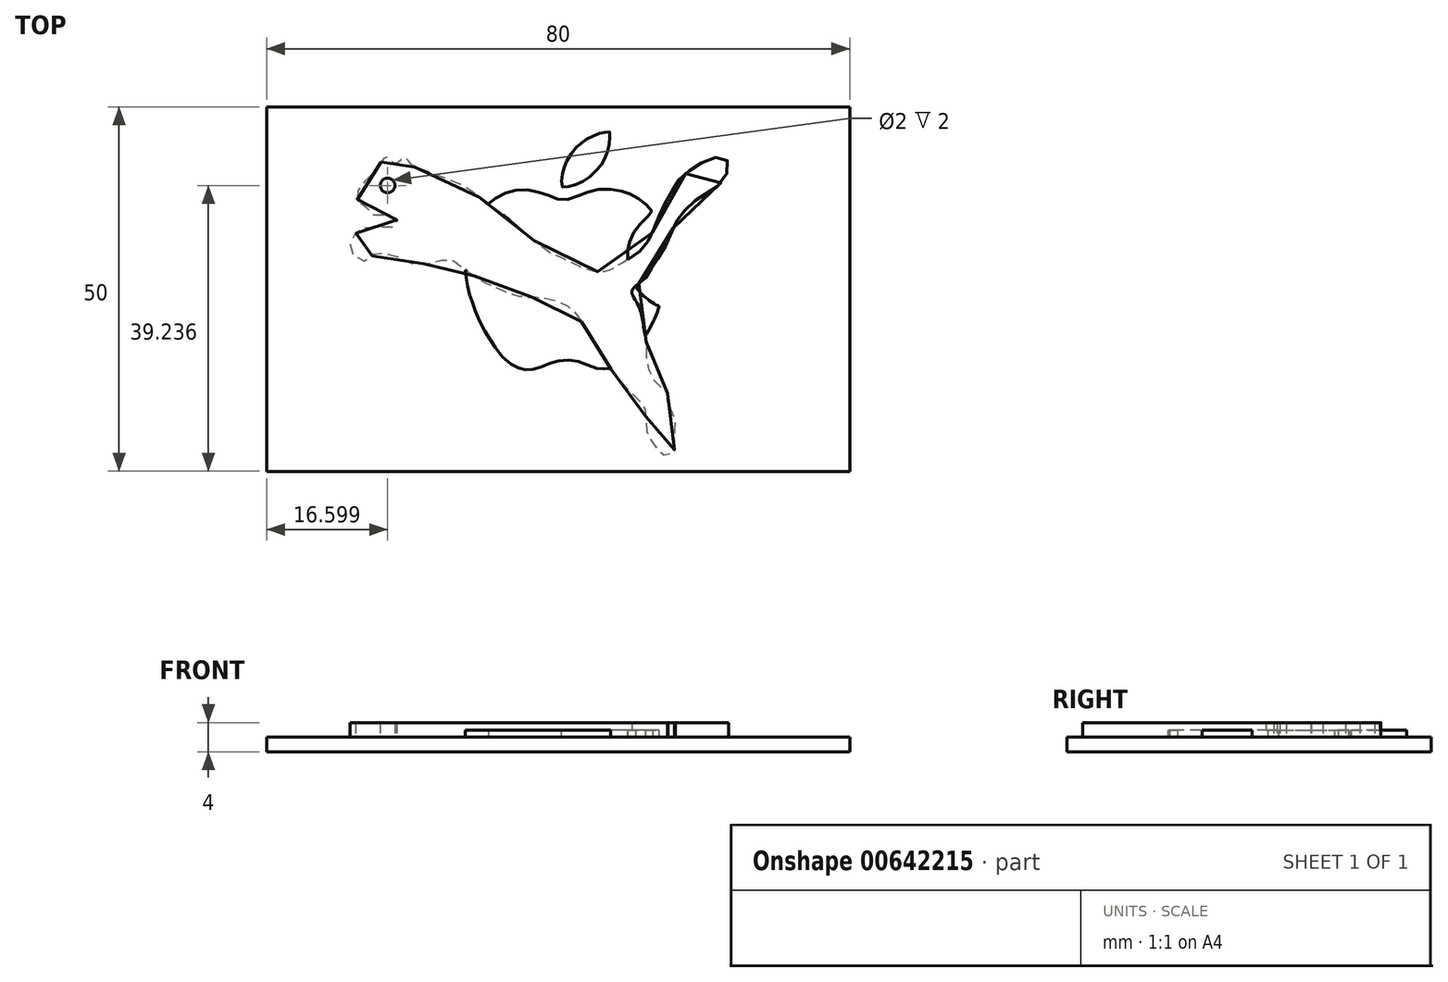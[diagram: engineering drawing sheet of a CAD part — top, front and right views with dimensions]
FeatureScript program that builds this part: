
annotation { "Feature Type Name" : "Feature", "Feature Type Description" : "" }
export const myFeature = defineFeature(function(context is Context, id is Id, definition is map)
    precondition{}
    {
        {
            var Q0;
            Q0=qCreatedBy(makeId("Top.planeOp"),FACE);
            var sketch = newSketch(context, id + "F0", { "sketchPlane" : qUnion([Q0])});
            skFitSpline(sketch, "E0", {"points": [v(-22.96, 25.7) * mm, v(-24.03, 24.14) * mm, v(-25, 23.44) * mm, v(-25.24, 22.78) * mm, v(-25.97, 21.9) * mm, v(-26.4, 21.24) * mm, v(-26.11, 20.44) * mm, v(-25.38, 19.78) * mm, v(-24.65, 19.13) * mm, v(-24.01, 18.5) * mm, v(-22.1, 18.4) * mm, v(-20.93, 18.18) * mm, v(-20.78, 17.23) * mm, v(-21, 16.79) * mm, v(-22.17, 16.79) * mm, v(-24, 16.72) * mm, v(-25.09, 16.64) * mm, v(-26.11, 16.06) * mm, v(-26.84, 15.55) * mm, v(-27.2, 14.38) * mm, v(-26.99, 13.14) * mm, v(-26.11, 12.48) * mm, v(-24.94, 12.12) * mm, v(-24.07, 12.92) * mm, v(-23.63, 13.36) * mm, v(-21.84, 13.01) * mm, v(-20.44, 12.57) * mm, v(-18.88, 11.82) * mm, v(-16.72, 11.72) * mm, v(-15.1, 12.05) * mm, v(-13.48, 12.48) * mm, v(-12.31, 11.53) * mm, v(-10.93, 10.58) * mm, v(-9.68, 9.7) * mm, v(-8.22, 8.9) * mm, v(-6.18, 8.03) * mm, v(-4.14, 7.3) * mm, v(-1.87, 7.15) * mm, v(0, 6.93) * mm, v(1.7, 6.42) * mm, v(3.16, 5.55) * mm, v(4.19, 4.3) * mm, v(5.06, 3) * mm, v(6.01, 1.31) * mm, v(6.82, 0) * mm, v(7.7, -1.39) * mm, v(8.5, -2.56) * mm, v(9.55, -3.97) * mm, v(10.78, -5.38) * mm, v(12.45, -7.06) * mm, v(13.25, -8.11) * mm, v(13.42, -10.14) * mm, v(13.69, -11.81) * mm, v(14.66, -13.22) * mm, v(15.63, -14.46) * mm, v(17.12, -14.2) * mm, v(17.3, -12.43) * mm, v(17.48, -10.5) * mm, v(17.12, -8.82) * mm, v(16.42, -7.59) * mm, v(16.33, -5.91) * mm, v(15.45, -5.2) * mm, v(14.4, -4.15) * mm, v(13.6, -1.86) * mm, v(13.51, 0) * mm, v(13.25, 2.1) * mm, v(12.9, 4.22) * mm, v(12.28, 6.16) * mm, v(11.49, 8) * mm, v(13.06, 9.5) * mm, v(14.01, 10.81) * mm, v(14.82, 12.13) * mm, v(16.36, 14.66) * mm, v(17.3, 17.03) * mm, v(18.38, 18.6) * mm, v(20.24, 20.48) * mm, v(21.9, 21.47) * mm, v(24.13, 23.39) * mm, v(24.63, 25.82) * mm, v(22.75, 26.26) * mm, v(20.08, 24.99) * mm, v(18.17, 23.5) * mm, v(16.9, 21.58) * mm, v(15.61, 19.24) * mm, v(14.76, 17.22) * mm, v(13.7, 14.77) * mm, v(12.1, 13.07) * mm, v(9.55, 11.47) * mm, v(7.5, 10.6) * mm, v(4.01, 11.47) * mm, v(1.35, 12.75) * mm, v(0, 13.39) * mm, v(-1.73, 14.77) * mm, v(-3.14, 15.83) * mm, v(-5.35, 17.75) * mm, v(-7.37, 19.35) * mm, v(-9.66, 21.04) * mm, v(-11.63, 22.43) * mm, v(-13.97, 23.39) * mm, v(-16.74, 24.45) * mm, v(-18.87, 25.41) * mm, v(-19.61, 26.26) * mm, v(-20.46, 25.73) * mm, v(-21.12, 25.53) * mm, v(-21.8, 26) * mm, v(-22.25, 26.34) * mm, v(-22.96, 25.7) * mm]});
            skCircle(sketch, "E1", {"center": v(-22.04, 22.48) * mm, "radius": 0.08 * mm});
            skSolve(sketch);
        }
        {
            var Q0;
            Q0 = qSketchRegion(id + "F0", true);
            extrude(context, id + "F1", {"entities" : qUnion([Q0]), "depth" : 4 * mm, "offsetDistance" : 25 * mm});
        }
        {
            var Q0;
            Q0=sQuery(id+"F0.wireOp",VERTEX,"E1.center");
            var Q1;
            Q1=makeQuery(id+"F1.opExtrude","SWEPT_BODY",BODY,{"disambiguationData":[OSD([sQuery(id+"F0.wireOp",EDGE,"E0"),sQuery(id+"F0.wireOp",EDGE,"b66a4d29-bf38-48c4-a418-0a1d268e2e5a.sketch_text.stroke-0"),sQuery(id+"F0.wireOp",EDGE,"b66a4d29-bf38-48c4-a418-0a1d268e2e5a.sketch_text.stroke-1"),sQuery(id+"F0.wireOp",EDGE,"b66a4d29-bf38-48c4-a418-0a1d268e2e5a.sketch_text.stroke-2"),sQuery(id+"F0.wireOp",EDGE,"b66a4d29-bf38-48c4-a418-0a1d268e2e5a.sketch_text.stroke-3"),sQuery(id+"F0.wireOp",EDGE,"b66a4d29-bf38-48c4-a418-0a1d268e2e5a.sketch_text.stroke-4"),sQuery(id+"F0.wireOp",EDGE,"b66a4d29-bf38-48c4-a418-0a1d268e2e5a.sketch_text.stroke-5"),sQuery(id+"F0.wireOp",EDGE,"b66a4d29-bf38-48c4-a418-0a1d268e2e5a.sketch_text.stroke-6"),sQuery(id+"F0.wireOp",EDGE,"b66a4d29-bf38-48c4-a418-0a1d268e2e5a.sketch_text.stroke-7"),sQuery(id+"F0.wireOp",EDGE,"b66a4d29-bf38-48c4-a418-0a1d268e2e5a.sketch_text.stroke-8"),sQuery(id+"F0.wireOp",EDGE,"b66a4d29-bf38-48c4-a418-0a1d268e2e5a.sketch_text.stroke-9"),sQuery(id+"F0.wireOp",EDGE,"b66a4d29-bf38-48c4-a418-0a1d268e2e5a.sketch_text.stroke-10"),sQuery(id+"F0.wireOp",EDGE,"b66a4d29-bf38-48c4-a418-0a1d268e2e5a.sketch_text.stroke-11"),sQuery(id+"F0.wireOp",EDGE,"b66a4d29-bf38-48c4-a418-0a1d268e2e5a.sketch_text.stroke-12"),sQuery(id+"F0.wireOp",EDGE,"b66a4d29-bf38-48c4-a418-0a1d268e2e5a.sketch_text.stroke-13"),sQuery(id+"F0.wireOp",EDGE,"b66a4d29-bf38-48c4-a418-0a1d268e2e5a.sketch_text.stroke-14"),sQuery(id+"F0.wireOp",EDGE,"b66a4d29-bf38-48c4-a418-0a1d268e2e5a.sketch_text.stroke-15"),sQuery(id+"F0.wireOp",EDGE,"b66a4d29-bf38-48c4-a418-0a1d268e2e5a.sketch_text.stroke-23"),sQuery(id+"F0.wireOp",EDGE,"b66a4d29-bf38-48c4-a418-0a1d268e2e5a.sketch_text.stroke-24"),sQuery(id+"F0.wireOp",EDGE,"b66a4d29-bf38-48c4-a418-0a1d268e2e5a.sketch_text.stroke-25"),sQuery(id+"F0.wireOp",EDGE,"b66a4d29-bf38-48c4-a418-0a1d268e2e5a.sketch_text.stroke-26"),sQuery(id+"F0.wireOp",EDGE,"b66a4d29-bf38-48c4-a418-0a1d268e2e5a.sketch_text.stroke-27"),sQuery(id+"F0.wireOp",EDGE,"b66a4d29-bf38-48c4-a418-0a1d268e2e5a.sketch_text.stroke-28"),sQuery(id+"F0.wireOp",EDGE,"b66a4d29-bf38-48c4-a418-0a1d268e2e5a.sketch_text.stroke-29"),sQuery(id+"F0.wireOp",EDGE,"b66a4d29-bf38-48c4-a418-0a1d268e2e5a.sketch_text.stroke-30"),sQuery(id+"F0.wireOp",EDGE,"b66a4d29-bf38-48c4-a418-0a1d268e2e5a.sketch_text.stroke-31"),sQuery(id+"F0.wireOp",EDGE,"b66a4d29-bf38-48c4-a418-0a1d268e2e5a.sketch_text.stroke-32"),sQuery(id+"F0.wireOp",EDGE,"b66a4d29-bf38-48c4-a418-0a1d268e2e5a.sketch_text.stroke-33"),sQuery(id+"F0.wireOp",EDGE,"b66a4d29-bf38-48c4-a418-0a1d268e2e5a.sketch_text.stroke-34"),sQuery(id+"F0.wireOp",EDGE,"b66a4d29-bf38-48c4-a418-0a1d268e2e5a.sketch_text.stroke-35"),sQuery(id+"F0.wireOp",EDGE,"b66a4d29-bf38-48c4-a418-0a1d268e2e5a.sketch_text.stroke-36"),sQuery(id+"F0.wireOp",EDGE,"b66a4d29-bf38-48c4-a418-0a1d268e2e5a.sketch_text.stroke-37"),sQuery(id+"F0.wireOp",EDGE,"b66a4d29-bf38-48c4-a418-0a1d268e2e5a.sketch_text.stroke-38"),sQuery(id+"F0.wireOp",EDGE,"b66a4d29-bf38-48c4-a418-0a1d268e2e5a.sketch_text.stroke-39"),sQuery(id+"F0.wireOp",EDGE,"b66a4d29-bf38-48c4-a418-0a1d268e2e5a.sketch_text.stroke-40"),sQuery(id+"F0.wireOp",EDGE,"b66a4d29-bf38-48c4-a418-0a1d268e2e5a.sketch_text.stroke-41"),sQuery(id+"F0.wireOp",EDGE,"b66a4d29-bf38-48c4-a418-0a1d268e2e5a.sketch_text.stroke-42"),sQuery(id+"F0.wireOp",EDGE,"b66a4d29-bf38-48c4-a418-0a1d268e2e5a.sketch_text.stroke-43"),sQuery(id+"F0.wireOp",EDGE,"b66a4d29-bf38-48c4-a418-0a1d268e2e5a.sketch_text.stroke-44"),sQuery(id+"F0.wireOp",EDGE,"b66a4d29-bf38-48c4-a418-0a1d268e2e5a.sketch_text.stroke-45"),sQuery(id+"F0.wireOp",EDGE,"b66a4d29-bf38-48c4-a418-0a1d268e2e5a.sketch_text.stroke-46"),sQuery(id+"F0.wireOp",EDGE,"b66a4d29-bf38-48c4-a418-0a1d268e2e5a.sketch_text.stroke-47"),sQuery(id+"F0.wireOp",EDGE,"b66a4d29-bf38-48c4-a418-0a1d268e2e5a.sketch_text.stroke-48"),sQuery(id+"F0.wireOp",EDGE,"b66a4d29-bf38-48c4-a418-0a1d268e2e5a.sketch_text.stroke-49"),sQuery(id+"F0.wireOp",EDGE,"b66a4d29-bf38-48c4-a418-0a1d268e2e5a.sketch_text.stroke-50"),sQuery(id+"F0.wireOp",EDGE,"b66a4d29-bf38-48c4-a418-0a1d268e2e5a.sketch_text.stroke-51"),sQuery(id+"F0.wireOp",EDGE,"b66a4d29-bf38-48c4-a418-0a1d268e2e5a.sketch_text.stroke-52"),sQuery(id+"F0.wireOp",EDGE,"b66a4d29-bf38-48c4-a418-0a1d268e2e5a.sketch_text.stroke-53"),sQuery(id+"F0.wireOp",EDGE,"b66a4d29-bf38-48c4-a418-0a1d268e2e5a.sketch_text.stroke-54"),sQuery(id+"F0.wireOp",EDGE,"b66a4d29-bf38-48c4-a418-0a1d268e2e5a.sketch_text.stroke-55"),sQuery(id+"F0.wireOp",EDGE,"b66a4d29-bf38-48c4-a418-0a1d268e2e5a.sketch_text.stroke-56"),sQuery(id+"F0.wireOp",EDGE,"b66a4d29-bf38-48c4-a418-0a1d268e2e5a.sketch_text.stroke-57"),sQuery(id+"F0.wireOp",EDGE,"b66a4d29-bf38-48c4-a418-0a1d268e2e5a.sketch_text.stroke-58"),sQuery(id+"F0.wireOp",EDGE,"b66a4d29-bf38-48c4-a418-0a1d268e2e5a.sketch_text.stroke-59"),sQuery(id+"F0.wireOp",EDGE,"b66a4d29-bf38-48c4-a418-0a1d268e2e5a.sketch_text.stroke-60"),sQuery(id+"F0.wireOp",EDGE,"b66a4d29-bf38-48c4-a418-0a1d268e2e5a.sketch_text.stroke-61"),sQuery(id+"F0.wireOp",EDGE,"b66a4d29-bf38-48c4-a418-0a1d268e2e5a.sketch_text.stroke-62"),sQuery(id+"F0.wireOp",EDGE,"b66a4d29-bf38-48c4-a418-0a1d268e2e5a.sketch_text.stroke-63"),sQuery(id+"F0.wireOp",EDGE,"b66a4d29-bf38-48c4-a418-0a1d268e2e5a.sketch_text.stroke-64"),sQuery(id+"F0.wireOp",EDGE,"b66a4d29-bf38-48c4-a418-0a1d268e2e5a.sketch_text.stroke-65"),sQuery(id+"F0.wireOp",EDGE,"b66a4d29-bf38-48c4-a418-0a1d268e2e5a.sketch_text.stroke-66"),sQuery(id+"F0.wireOp",EDGE,"b66a4d29-bf38-48c4-a418-0a1d268e2e5a.sketch_text.stroke-67"),sQuery(id+"F0.wireOp",EDGE,"b66a4d29-bf38-48c4-a418-0a1d268e2e5a.sketch_text.stroke-68"),sQuery(id+"F0.wireOp",EDGE,"b66a4d29-bf38-48c4-a418-0a1d268e2e5a.sketch_text.stroke-69"),sQuery(id+"F0.wireOp",EDGE,"b66a4d29-bf38-48c4-a418-0a1d268e2e5a.sketch_text.stroke-70"),sQuery(id+"F0.wireOp",EDGE,"b66a4d29-bf38-48c4-a418-0a1d268e2e5a.sketch_text.stroke-71"),sQuery(id+"F0.wireOp",EDGE,"b66a4d29-bf38-48c4-a418-0a1d268e2e5a.sketch_text.stroke-72"),sQuery(id+"F0.wireOp",EDGE,"b66a4d29-bf38-48c4-a418-0a1d268e2e5a.sketch_text.stroke-73"),sQuery(id+"F0.wireOp",EDGE,"b66a4d29-bf38-48c4-a418-0a1d268e2e5a.sketch_text.stroke-74"),sQuery(id+"F0.wireOp",EDGE,"b66a4d29-bf38-48c4-a418-0a1d268e2e5a.sketch_text.stroke-75"),sQuery(id+"F0.wireOp",EDGE,"b66a4d29-bf38-48c4-a418-0a1d268e2e5a.sketch_text.stroke-76"),sQuery(id+"F0.wireOp",EDGE,"b66a4d29-bf38-48c4-a418-0a1d268e2e5a.sketch_text.stroke-77"),sQuery(id+"F0.wireOp",EDGE,"b66a4d29-bf38-48c4-a418-0a1d268e2e5a.sketch_text.stroke-78"),sQuery(id+"F0.wireOp",EDGE,"b66a4d29-bf38-48c4-a418-0a1d268e2e5a.sketch_text.stroke-79"),sQuery(id+"F0.wireOp",EDGE,"b66a4d29-bf38-48c4-a418-0a1d268e2e5a.sketch_text.stroke-80"),sQuery(id+"F0.wireOp",EDGE,"b66a4d29-bf38-48c4-a418-0a1d268e2e5a.sketch_text.stroke-81"),sQuery(id+"F0.wireOp",EDGE,"b66a4d29-bf38-48c4-a418-0a1d268e2e5a.sketch_text.stroke-82"),sQuery(id+"F0.wireOp",EDGE,"b66a4d29-bf38-48c4-a418-0a1d268e2e5a.sketch_text.stroke-83"),sQuery(id+"F0.wireOp",EDGE,"b66a4d29-bf38-48c4-a418-0a1d268e2e5a.sketch_text.stroke-84"),sQuery(id+"F0.wireOp",EDGE,"b66a4d29-bf38-48c4-a418-0a1d268e2e5a.sketch_text.stroke-85"),sQuery(id+"F0.wireOp",EDGE,"b66a4d29-bf38-48c4-a418-0a1d268e2e5a.sketch_text.stroke-86"),sQuery(id+"F0.wireOp",EDGE,"b66a4d29-bf38-48c4-a418-0a1d268e2e5a.sketch_text.stroke-87"),sQuery(id+"F0.wireOp",EDGE,"b66a4d29-bf38-48c4-a418-0a1d268e2e5a.sketch_text.stroke-88"),sQuery(id+"F0.wireOp",EDGE,"b66a4d29-bf38-48c4-a418-0a1d268e2e5a.sketch_text.stroke-89"),sQuery(id+"F0.wireOp",EDGE,"b66a4d29-bf38-48c4-a418-0a1d268e2e5a.sketch_text.stroke-90"),sQuery(id+"F0.wireOp",EDGE,"b66a4d29-bf38-48c4-a418-0a1d268e2e5a.sketch_text.stroke-91"),sQuery(id+"F0.wireOp",EDGE,"b66a4d29-bf38-48c4-a418-0a1d268e2e5a.sketch_text.stroke-92"),sQuery(id+"F0.wireOp",EDGE,"b66a4d29-bf38-48c4-a418-0a1d268e2e5a.sketch_text.stroke-93"),sQuery(id+"F0.wireOp",EDGE,"b66a4d29-bf38-48c4-a418-0a1d268e2e5a.sketch_text.stroke-94"),sQuery(id+"F0.wireOp",EDGE,"b66a4d29-bf38-48c4-a418-0a1d268e2e5a.sketch_text.stroke-95"),sQuery(id+"F0.wireOp",EDGE,"b66a4d29-bf38-48c4-a418-0a1d268e2e5a.sketch_text.stroke-96"),sQuery(id+"F0.wireOp",EDGE,"b66a4d29-bf38-48c4-a418-0a1d268e2e5a.sketch_text.stroke-97"),sQuery(id+"F0.wireOp",EDGE,"b66a4d29-bf38-48c4-a418-0a1d268e2e5a.sketch_text.stroke-98"),sQuery(id+"F0.wireOp",EDGE,"b66a4d29-bf38-48c4-a418-0a1d268e2e5a.sketch_text.stroke-99"),sQuery(id+"F0.wireOp",EDGE,"b66a4d29-bf38-48c4-a418-0a1d268e2e5a.sketch_text.stroke-100"),sQuery(id+"F0.wireOp",EDGE,"b66a4d29-bf38-48c4-a418-0a1d268e2e5a.sketch_text.stroke-101"),sQuery(id+"F0.wireOp",EDGE,"b66a4d29-bf38-48c4-a418-0a1d268e2e5a.sketch_text.stroke-102"),sQuery(id+"F0.wireOp",EDGE,"b66a4d29-bf38-48c4-a418-0a1d268e2e5a.sketch_text.stroke-103"),sQuery(id+"F0.wireOp",EDGE,"b66a4d29-bf38-48c4-a418-0a1d268e2e5a.sketch_text.stroke-104"),sQuery(id+"F0.wireOp",EDGE,"b66a4d29-bf38-48c4-a418-0a1d268e2e5a.sketch_text.stroke-105"),sQuery(id+"F0.wireOp",EDGE,"b66a4d29-bf38-48c4-a418-0a1d268e2e5a.sketch_text.stroke-106"),sQuery(id+"F0.wireOp",EDGE,"b66a4d29-bf38-48c4-a418-0a1d268e2e5a.sketch_text.stroke-107"),sQuery(id+"F0.wireOp",EDGE,"b66a4d29-bf38-48c4-a418-0a1d268e2e5a.sketch_text.stroke-108"),sQuery(id+"F0.wireOp",EDGE,"b66a4d29-bf38-48c4-a418-0a1d268e2e5a.sketch_text.stroke-109"),sQuery(id+"F0.wireOp",EDGE,"b66a4d29-bf38-48c4-a418-0a1d268e2e5a.sketch_text.stroke-110"),sQuery(id+"F0.wireOp",EDGE,"b66a4d29-bf38-48c4-a418-0a1d268e2e5a.sketch_text.stroke-111"),sQuery(id+"F0.wireOp",EDGE,"b66a4d29-bf38-48c4-a418-0a1d268e2e5a.sketch_text.stroke-112"),sQuery(id+"F0.wireOp",EDGE,"b66a4d29-bf38-48c4-a418-0a1d268e2e5a.sketch_text.stroke-113"),sQuery(id+"F0.wireOp",EDGE,"b66a4d29-bf38-48c4-a418-0a1d268e2e5a.sketch_text.stroke-114"),sQuery(id+"F0.wireOp",EDGE,"b66a4d29-bf38-48c4-a418-0a1d268e2e5a.sketch_text.stroke-115"),sQuery(id+"F0.wireOp",EDGE,"b66a4d29-bf38-48c4-a418-0a1d268e2e5a.sketch_text.stroke-116"),sQuery(id+"F0.wireOp",EDGE,"E1")])]});
            hole(context, id + "F2", {"style" : HoleStyle.SIMPLE, "endStyle" : HoleEndStyle.THROUGH, "oppositeDirection" : true, "holeDiameter" : 2 * mm, "majorDiameter" : 5 * mm, "isTappedThrough" : true, "tappedDepth" : 12 * mm, "tapClearance" : 3, "locations" : qUnion([Q0]), "scope" : qUnion([Q1])});
        }
        {
            var Q0;
            Q0=qCreatedBy(makeId("Top.planeOp"),FACE);
            var sketch = newSketch(context, id + "F3", { "sketchPlane" : qUnion([Q0])});
            skLineSegment(sketch, "E2.bottom", {"start": v(-38.64, 33.24) * mm, "end": v(41.36, 33.24) * mm});
            skLineSegment(sketch, "E2.top", {"start": v(-38.64, -16.76) * mm, "end": v(41.36, -16.76) * mm});
            skLineSegment(sketch, "E2.left", {"start": v(-38.64, 33.24) * mm, "end": v(-38.64, -16.76) * mm});
            skLineSegment(sketch, "E2.right", {"start": v(41.36, 33.24) * mm, "end": v(41.36, -16.76) * mm});
            skSolve(sketch);
        }
        {
            var Q0;
            Q0 = qSketchRegion(id + "F3", true);
            extrude(context, id + "F4", {"entities" : qUnion([Q0]), "operationType" : NewBodyOperationType.ADD, "depth" : 2 * mm, "offsetDistance" : 25 * mm});
        }
        {
            var Q0;
            {var subQ0=sQuery(id+"F3.wireOp",EDGE,"E2.left");var subQ1=sQuery(id+"F3.wireOp",EDGE,"E2.top");var subQ2=sQuery(id+"F3.wireOp",EDGE,"E2.bottom");var subQ3=sQuery(id+"F3.wireOp",EDGE,"E2.right");Q0=makeQuery(id+"F4.boolean.opBoolean","SPLIT",FACE,{"disambiguationData":[TD([makeQuery(id+"F1.opExtrude","SWEPT_FACE",FACE,{"disambiguationData":[OSD([sQuery(id+"F0.wireOp",EDGE,"E0")])]})])],"derivedFrom":makeQuery(id+"F4.opExtrude","CAP_FACE",FACE,{"disambiguationData":[OSD([subQ2,subQ1,subQ0,subQ3])],"isStart":false})});}
            var sketch = newSketch(context, id + "F5", { "sketchPlane" : qUnion([Q0])});
            skFitSpline(sketch, "E3", {"points": [v(-7.75, 20.33) * mm, v(-8.21, 19.96) * mm, v(-8.77, 19.53) * mm, v(-9.32, 18.82) * mm, v(-10.06, 17.83) * mm, v(-10.5, 16.74) * mm, v(-10.86, 15.78) * mm, v(-11.27, 14.24) * mm, v(-11.34, 13.18) * mm, v(-11.36, 11.8) * mm, v(-11.36, 10.85) * mm, v(-11.24, 9.83) * mm, v(-11.04, 8.6) * mm, v(-10.77, 7.49) * mm, v(-10.43, 6.45) * mm, v(-9.82, 4.73) * mm, v(-8.95, 2.94) * mm, v(-7.93, 1.27) * mm, v(-7.12, 0) * mm, v(-5.45, -1.86) * mm, v(-4.21, -2.52) * mm, v(-3.38, -2.81) * mm, v(-2.51, -2.81) * mm, v(-1.46, -2.6) * mm, v(0, -2) * mm, v(1.32, -1.6) * mm, v(2.97, -1.5) * mm, v(4.69, -1.86) * mm, v(6.32, -2.52) * mm, v(7.23, -2.7) * mm, v(8.18, -2.7) * mm, v(8.8, -2.6) * mm, v(9.65, -2.33) * mm, v(10.53, -1.7) * mm, v(11.29, -1) * mm, v(11.7, -0.48) * mm, v(12.1, 0) * mm, v(12.57, 0.7) * mm, v(13.12, 1.46) * mm, v(13.3, 1.8) * mm, v(13.6, 2.27) * mm, v(14.06, 3.1) * mm, v(14.5, 4) * mm, v(14.87, 4.83) * mm, v(15.18, 5.7) * mm, v(15.2, 5.93) * mm, v(14.86, 6.03) * mm, v(14.53, 6.24) * mm, v(14.16, 6.49) * mm, v(13.67, 6.83) * mm, v(13.35, 7.08) * mm, v(13.02, 7.4) * mm, v(12.67, 7.74) * mm, v(12.33, 8.11) * mm, v(11.96, 8.65) * mm, v(11.5, 9.65) * mm, v(11.13, 10.54) * mm, v(10.89, 11.76) * mm, v(10.88, 12.27) * mm, v(10.86, 13.06) * mm, v(11.02, 14.02) * mm, v(11.13, 14.54) * mm, v(11.47, 15.4) * mm, v(12, 16.45) * mm, v(12.65, 17.22) * mm, v(13.45, 18.05) * mm, v(14.34, 18.67) * mm, v(14.33, 18.78) * mm, v(13.87, 19.32) * mm, v(13.46, 19.82) * mm, v(12.79, 20.36) * mm, v(11.93, 20.97) * mm, v(11.21, 21.29) * mm, v(10.66, 21.55) * mm, v(9.54, 21.82) * mm, v(8.42, 21.95) * mm, v(6.95, 21.94) * mm, v(5.75, 21.65) * mm, v(4.83, 21.34) * mm, v(3.83, 20.95) * mm, v(2.67, 20.55) * mm, v(1.8, 20.5) * mm, v(0.5, 20.85) * mm, v(0, 21.1) * mm, v(-1.11, 21.46) * mm, v(-2.17, 21.8) * mm, v(-3.58, 21.87) * mm, v(-4.67, 21.74) * mm, v(-5.7, 21.46) * mm, v(-6.63, 21.1) * mm, v(-7.75, 20.33) * mm]});
            skFitSpline(sketch, "E4", {"points": [v(2.53, 25.84) * mm, v(2.25, 25.14) * mm, v(1.98, 24.26) * mm, v(1.85, 23.38) * mm, v(1.85, 22.34) * mm, v(2.08, 22.3) * mm, v(2.94, 22.34) * mm, v(3.83, 22.6) * mm, v(4.98, 23.12) * mm, v(6, 23.94) * mm, v(6.94, 24.91) * mm, v(7.53, 25.77) * mm, v(7.86, 26.47) * mm, v(8.26, 27.6) * mm, v(8.43, 28.6) * mm, v(8.47, 29.45) * mm, v(8.42, 29.85) * mm, v(7.94, 29.78) * mm, v(7.47, 29.69) * mm, v(6.92, 29.57) * mm, v(6.02, 29.2) * mm, v(5.3, 28.84) * mm, v(4.6, 28.34) * mm, v(4.03, 27.84) * mm, v(3.26, 26.98) * mm, v(2.53, 25.84) * mm]});
            skSolve(sketch);
        }
        {
            var Q0;
            Q0 = qSketchRegion(id + "F5", true);
            extrude(context, id + "F6", {"entities" : qUnion([Q0]), "operationType" : NewBodyOperationType.ADD, "depth" : 1 * mm, "offsetDistance" : 25 * mm});
        }
    });
